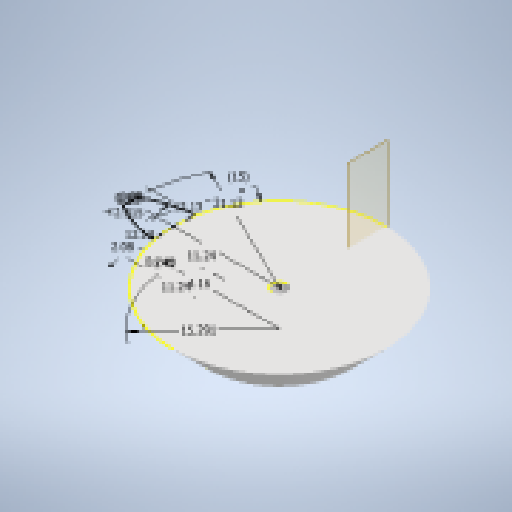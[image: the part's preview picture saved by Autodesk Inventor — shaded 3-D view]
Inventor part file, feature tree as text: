
AUTODESK INVENTOR PART (.ipt)
format: ipt  version: 2023 (Build 270158000, 158)  size: 367,104 bytes
history: native  units: in
note: dims shown in document units (in); Inventor stores cm internally (conversion verified against a paired STEP export)
features: sketch x2, other x1, plane x1, revolve x1, loft x1, pattern_circular x1
ambient origin geometry x8: Origin, YZ Plane, XZ Plane, XY Plane, X Axis, Y Axis, Z Axis, Center Point
bodies: Body1 (feature_tree)
feature tree (7):
  other  "bevelGear"
  plane  "Work Plane1"
  revolve  "Revolution1"  Angle=360.0deg
  loft  "Loft1"
  pattern_circular  "Circular Pattern1"  [2 undecoded]
  sketch  "Sketch2"  dims[d4=0.1969in d6=360.0deg]
  sketch  "Sketch3"  dims[d10=1.1811in d11=0.1969in d12=0.1969in d13=0.1969in d14=0.1969in d15=0.0423in d16=0.0846in d17=0.1638in d18=0.0819in d21=0.0293in d22=0.0559in d23=0.602in d24=0.4425in d25=0.4425in d26=0.1148in d27=0.2295in d29=0.0384in d30=0.0768in d31=0.5906in d32=0.8315in d33=0.4776in d34=0.4776in d35=0.0in d36=90.0deg d37=0.0in d38=90.0deg d39=3.937in d40=360.0deg]
note: 2 required parameter values undecoded (feature->parameter linkage not recoverable at this tier; creation-order binding heuristic only, values carry confidence <= 0.55)
